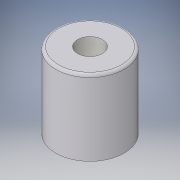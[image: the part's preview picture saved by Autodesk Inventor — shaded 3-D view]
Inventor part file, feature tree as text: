
AUTODESK INVENTOR PART (.ipt)
format: ipt  version: 2016 (Build 200138000, 138)  size: 131,584 bytes
history: native  units: in
note: dims shown in document units (in); Inventor stores cm internally (conversion verified against a paired STEP export)
features: extrude x2, sketch x2, fillet x1
ambient origin geometry x8: Origin, YZ Plane, XZ Plane, XY Plane, X Axis, Y Axis, Z Axis, Center Point
bodies: Solid1 (feature_tree)
feature tree (5):
  extrude  "Extrusion1"  Depth=0.2165in TaperAngle=0.0deg
  fillet  "Fillet1"  Radius=0.0079in
  extrude  "Extrusion2"  Depth=0.2362in TaperAngle=0.0deg
  sketch  "Sketch1"  dims[d0=0.1969in d1=0.2165in d2=0.0in d3=0.0079in]
  sketch  "Sketch2"  dims[d4=0.0709in d5=0.2362in d6=0.0in]
